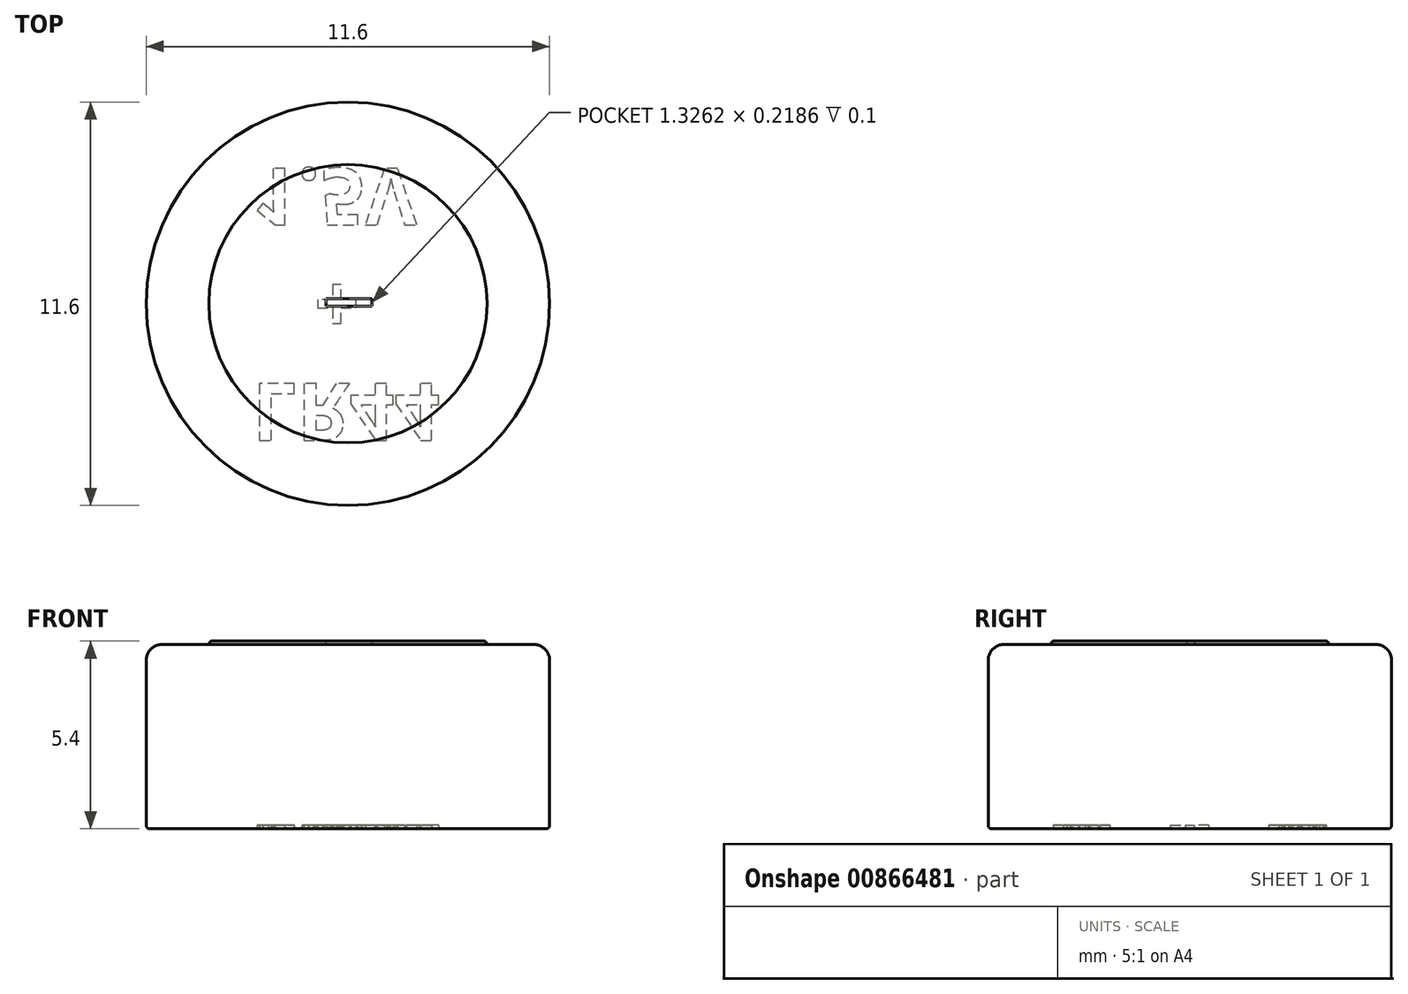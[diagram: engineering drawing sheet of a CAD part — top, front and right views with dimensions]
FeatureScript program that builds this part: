
annotation { "Feature Type Name" : "Feature", "Feature Type Description" : "" }
export const myFeature = defineFeature(function(context is Context, id is Id, definition is map)
    precondition{}
    {
        {
            var Q0;
            Q0=qCreatedBy(makeId("Top.planeOp"),FACE);
            var sketch = newSketch(context, id + "F0", { "sketchPlane" : qUnion([Q0])});
            skCircle(sketch, "E0", {"center": v(0, 0) * mm, "radius": 5.8 * mm});
            skSolve(sketch);
        }
        {
            var Q0;
            Q0 = qSketchRegion(id + "F0", true);
            extrude(context, id + "F1", {"entities" : qUnion([Q0]), "depth" : 5.3 * mm, "offsetDistance" : 25.4 * mm});
        }
        {
            var Q0;
            Q0=makeQuery(id+"F1.opExtrude","CAP_FACE",FACE,{"disambiguationData":[OSD([sQuery(id+"F0.wireOp",EDGE,"E0")])],"isStart":false});
            var sketch = newSketch(context, id + "F2", { "sketchPlane" : qUnion([Q0])});
            skCircle(sketch, "E1", {"center": v(0, 0) * mm, "radius": 4 * mm});
            skSolve(sketch);
        }
        {
            var Q0;
            Q0 = qSketchRegion(id + "F2", true);
            extrude(context, id + "F3", {"entities" : qUnion([Q0]), "operationType" : NewBodyOperationType.ADD, "depth" : .1 * mm, "offsetDistance" : 25.4 * mm});
        }
        {
            var Q0;
            Q0=makeQuery(id+"F3.opExtrude","CAP_EDGE",EDGE,{"disambiguationData":[OSD([sQuery(id+"F2.wireOp",EDGE,"E1")])],"isStart":false});
            fillet(context, id + "F4", {"entities" : qUnion([Q0]), "radius" : .1 * mm, "tangentPropagation" : true, "allowEdgeOverflow" : false});
        }
        {
            var Q0;
            Q0=makeQuery(id+"F1.opExtrude","CAP_EDGE",EDGE,{"disambiguationData":[OSD([sQuery(id+"F0.wireOp",EDGE,"E0")])],"isStart":false});
            fillet(context, id + "F5", {"entities" : qUnion([Q0]), "radius" : .45 * mm, "tangentPropagation" : true, "allowEdgeOverflow" : false});
        }
        {
            var Q0;
            Q0=makeQuery(id+"F1.opExtrude","CAP_EDGE",EDGE,{"disambiguationData":[OSD([sQuery(id+"F0.wireOp",EDGE,"E0")])],"isStart":true});
            fillet(context, id + "F6", {"entities" : qUnion([Q0]), "radius" : .1 * mm, "tangentPropagation" : true, "allowEdgeOverflow" : false});
        }
        {
            var Q0;
            Q0=makeQuery(id+"F3.opExtrude","CAP_FACE",FACE,{"disambiguationData":[OSD([sQuery(id+"F2.wireOp",EDGE,"E1")])],"isStart":false});
            var sketch = newSketch(context, id + "F7", { "sketchPlane" : qUnion([Q0])});
            skText(sketch, "E2", { "text": "_", "fontName": "OpenSans-Bold.ttf"});
            const initialGuessF7  = {"E2": [-0.00063, 0.00043, 1, 0, 0.0023]};
            skSetInitialGuess(sketch, initialGuessF7);
            skSolve(sketch);
        }
        {
            var Q0;
            Q0 = qSketchRegion(id + "F7", true);
            extrude(context, id + "F8", {"entities" : qUnion([Q0]), "operationType" : NewBodyOperationType.REMOVE, "oppositeDirection" : true, "depth" : .1 * mm, "offsetDistance" : 25.4 * mm});
        }
        {
            var Q0;
            Q0=makeQuery(id+"F1.opExtrude","CAP_FACE",FACE,{"disambiguationData":[OSD([sQuery(id+"F0.wireOp",EDGE,"E0")])],"isStart":true});
            var sketch = newSketch(context, id + "F9", { "sketchPlane" : qUnion([Q0])});
            skText(sketch, "E3", { "text": "LR44\n   +\n1.5V", "fontName": "OpenSans-Bold.ttf"});
            const initialGuessF9  = {"E3": [-0.00275, 0.0023, 1, 0, 0.00164]};
            skSetInitialGuess(sketch, initialGuessF9);
            skSolve(sketch);
        }
        {
            var Q0;
            Q0 = qSketchRegion(id + "F9", true);
            extrude(context, id + "F10", {"entities" : qUnion([Q0]), "operationType" : NewBodyOperationType.REMOVE, "oppositeDirection" : true, "depth" : .1 * mm, "offsetDistance" : 25.4 * mm});
        }
    });
